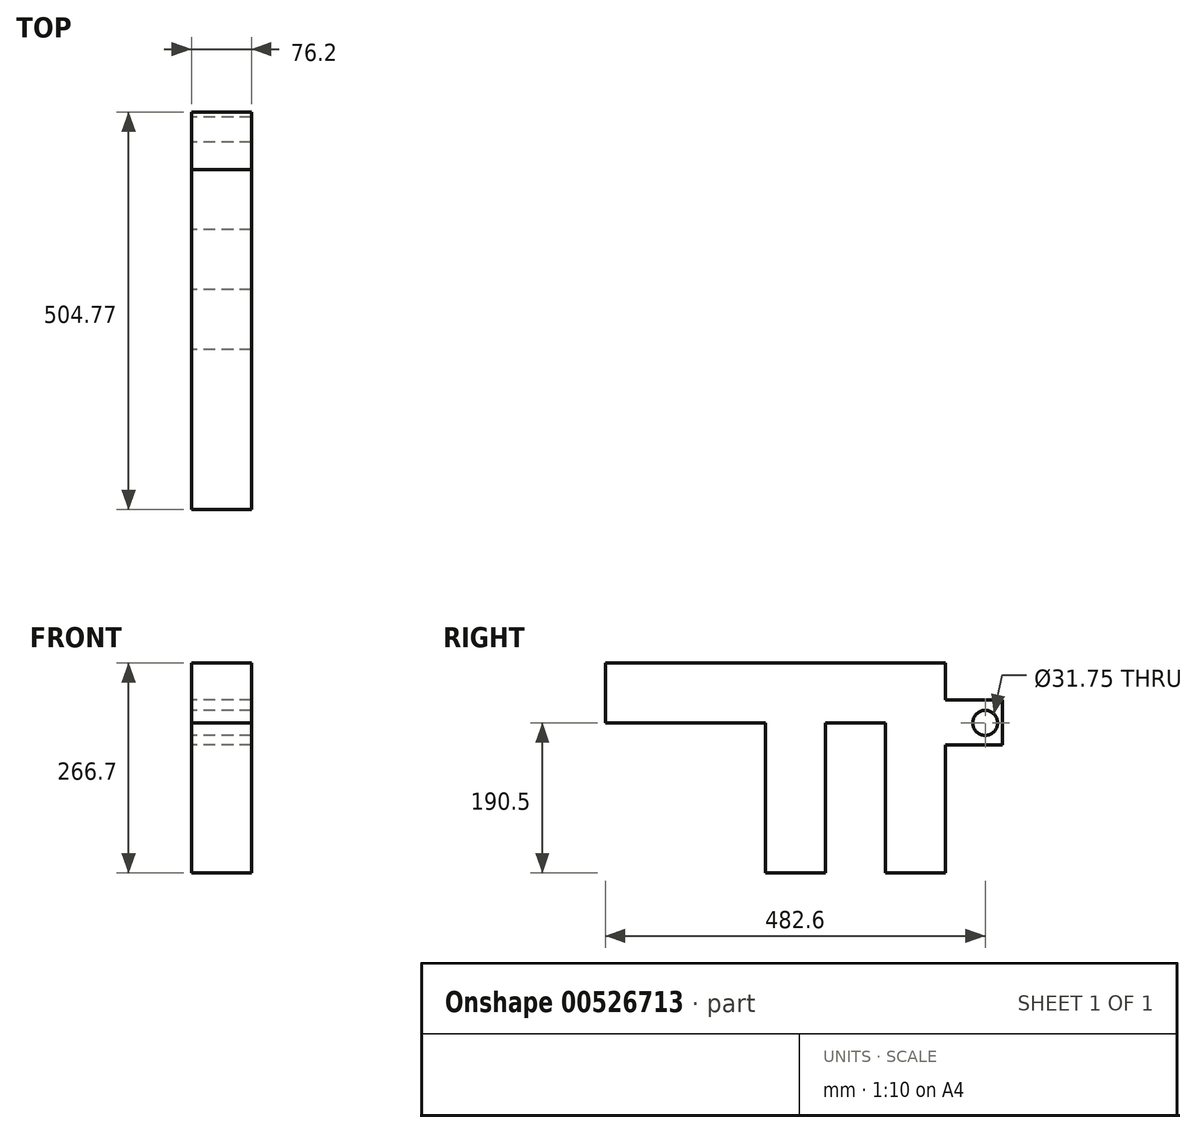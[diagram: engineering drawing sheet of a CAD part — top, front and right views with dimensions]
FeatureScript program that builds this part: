
annotation { "Feature Type Name" : "Feature", "Feature Type Description" : "" }
export const myFeature = defineFeature(function(context is Context, id is Id, definition is map)
    precondition{}
    {
        {
            var Q0;
            Q0=qCreatedBy(makeId("Right.planeOp"),FACE);
            var sketch = newSketch(context, id + "F0", { "sketchPlane" : qUnion([Q0])});
            skLineSegment(sketch, "E0", {"start": v(0, 0) * mm, "end": v(431.8, 0) * mm});
            skLineSegment(sketch, "E1", {"start": v(431.8, -266.7) * mm, "end": v(355.6, -266.7) * mm});
            skLineSegment(sketch, "E2", {"start": v(355.6, -266.7) * mm, "end": v(355.6, -76.2) * mm});
            skLineSegment(sketch, "E3", {"start": v(355.6, -76.2) * mm, "end": v(279.4, -76.2) * mm});
            skLineSegment(sketch, "E4", {"start": v(279.4, -76.2) * mm, "end": v(279.4, -266.7) * mm});
            skLineSegment(sketch, "E5", {"start": v(279.4, -266.7) * mm, "end": v(203.2, -266.7) * mm});
            skLineSegment(sketch, "E6", {"start": v(203.2, -266.7) * mm, "end": v(203.2, -76.2) * mm});
            skLineSegment(sketch, "E7", {"start": v(203.2, -76.2) * mm, "end": v(0, -76.2) * mm});
            skLineSegment(sketch, "E8", {"start": v(0, -76.2) * mm, "end": v(0, 0) * mm});
            skCircle(sketch, "E9", {"center": v(482.6, -76.2) * mm, "radius": 15.88 * mm});
            skLineSegment(sketch, "E10", {"start": v(431.8, -46.96) * mm, "end": v(504.77, -46.96) * mm});
            skLineSegment(sketch, "E11", {"start": v(504.77, -46.96) * mm, "end": v(504.77, -104.38) * mm});
            skLineSegment(sketch, "E12", {"start": v(504.77, -104.38) * mm, "end": v(431.8, -104.38) * mm});
            skLineSegment(sketch, "E13", {"start": v(431.8, 0) * mm, "end": v(431.8, -46.96) * mm});
            skLineSegment(sketch, "E14", {"start": v(431.8, -104.38) * mm, "end": v(431.8, -266.7) * mm});
            skSolve(sketch);
        }
        {
            var Q0;
            Q0=makeQuery(id+"F0.imprint","IMPRINT",FACE,{"disambiguationData":[TD([[makeQuery(id+"F0.imprint","IMPRINT",EDGE,{"derivedFrom":sQuery(id+"F0.wireOp",EDGE,"E0")}),-1.0]])]});
            extrude(context, id + "F1", {"entities" : qUnion([Q0]), "depth" : 76.2 * mm, "offsetDistance" : 25.4 * mm});
        }
    });
